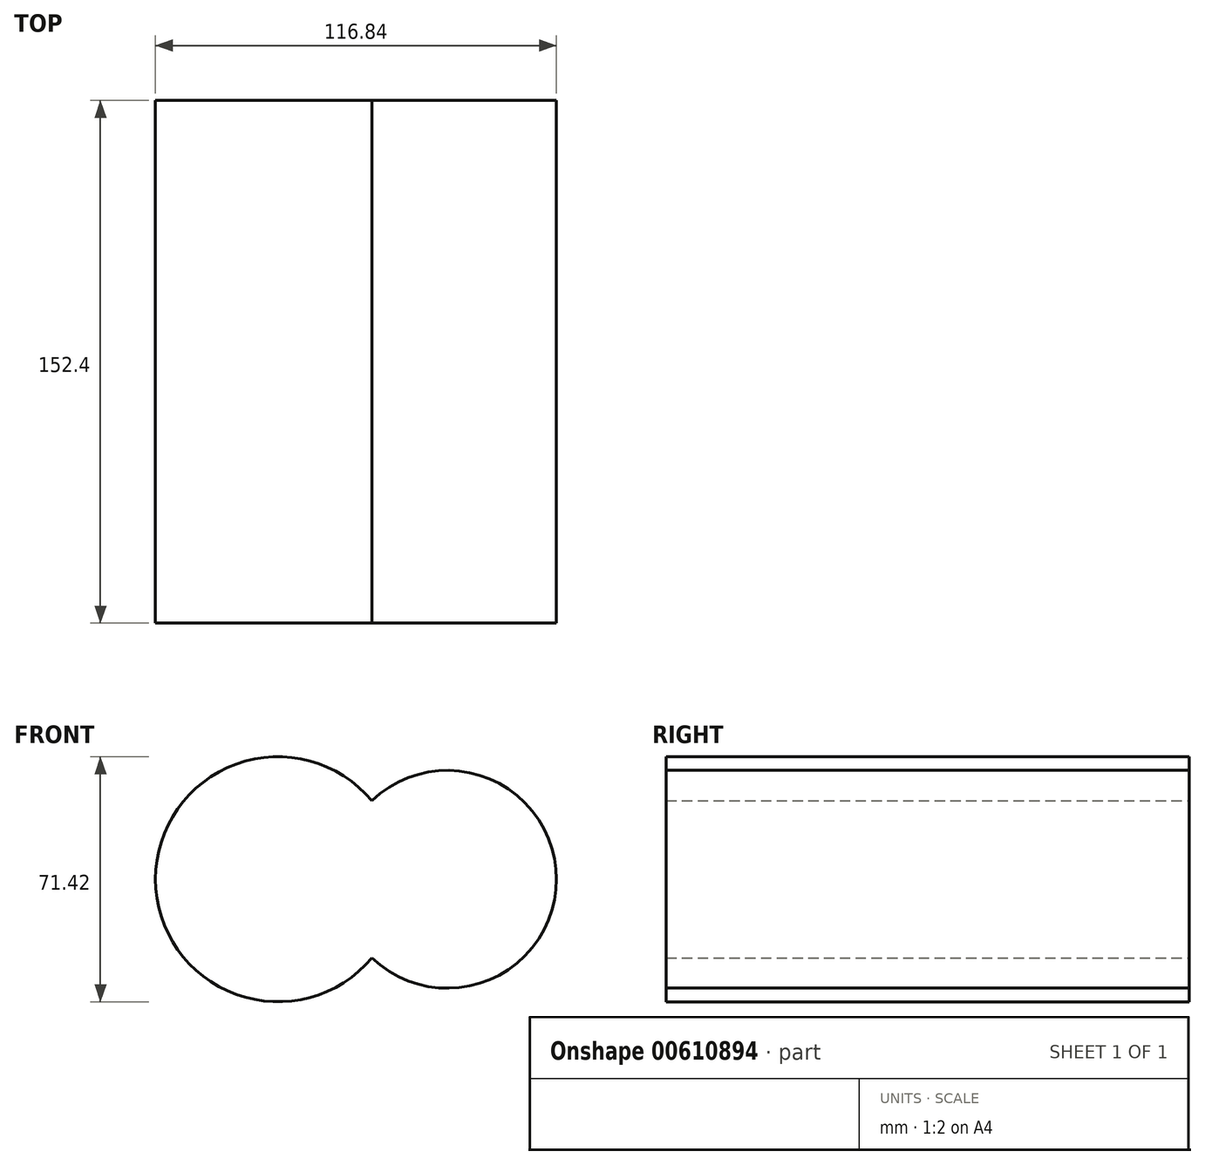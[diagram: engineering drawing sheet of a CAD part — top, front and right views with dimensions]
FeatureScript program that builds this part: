
annotation { "Feature Type Name" : "Feature", "Feature Type Description" : "" }
export const myFeature = defineFeature(function(context is Context, id is Id, definition is map)
    precondition{}
    {
        {
            var Q0;
            Q0=qCreatedBy(makeId("Front.planeOp"),FACE);
            var sketch = newSketch(context, id + "F0", { "sketchPlane" : qUnion([Q0])});
            skCircle(sketch, "E0", {"center": v(-17.63, 0) * mm, "radius": 35.7 * mm});
            skCircle(sketch, "E1", {"center": v(31.75, 0) * mm, "radius": 31.75 * mm});
            skSolve(sketch);
        }
        {
            var Q0;
            Q0 = qSketchRegion(id + "F0", true);
            extrude(context, id + "F1", {"entities" : qUnion([Q0]), "depth" : 152.4 * mm, "offsetDistance" : 25.4 * mm});
        }
    });
